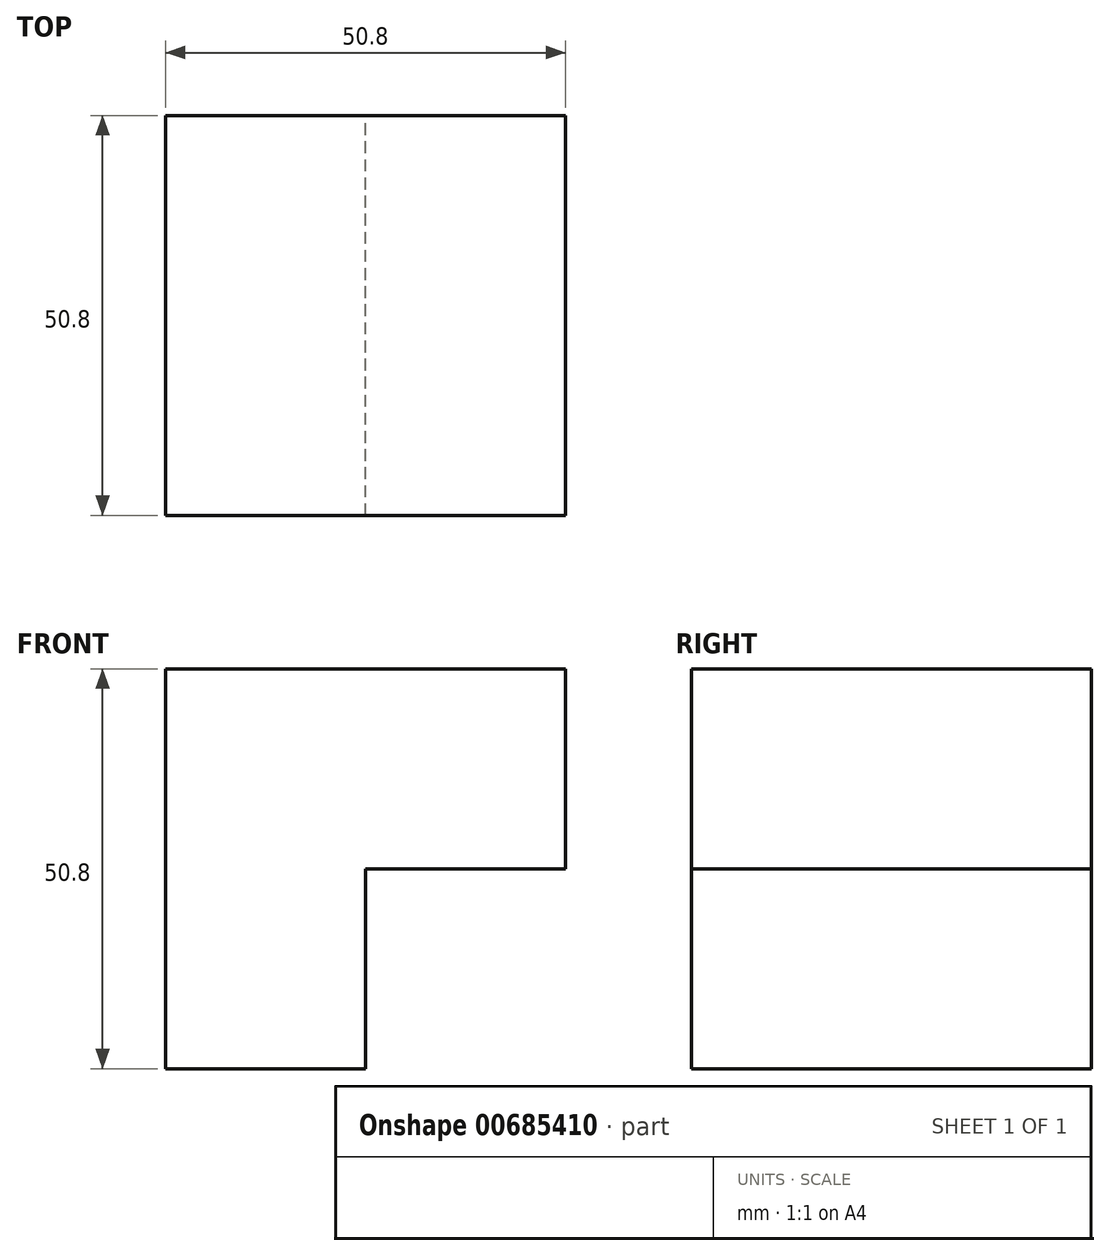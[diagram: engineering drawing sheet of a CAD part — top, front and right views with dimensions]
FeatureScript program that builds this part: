
annotation { "Feature Type Name" : "Feature", "Feature Type Description" : "" }
export const myFeature = defineFeature(function(context is Context, id is Id, definition is map)
    precondition{}
    {
        {
            var Q0;
            Q0=qCreatedBy(makeId("Front.planeOp"),FACE);
            var sketch = newSketch(context, id + "F0", { "sketchPlane" : qUnion([Q0])});
            skLineSegment(sketch, "E0", {"start": v(0, 0) * mm, "end": v(0, 50.8) * mm});
            skLineSegment(sketch, "E1", {"start": v(0, 50.8) * mm, "end": v(50.8, 50.8) * mm});
            skLineSegment(sketch, "E2", {"start": v(50.8, 50.8) * mm, "end": v(50.8, 25.4) * mm});
            skLineSegment(sketch, "E3", {"start": v(50.8, 25.4) * mm, "end": v(25.4, 25.4) * mm});
            skLineSegment(sketch, "E4", {"start": v(25.4, 25.4) * mm, "end": v(25.4, 0) * mm});
            skLineSegment(sketch, "E5", {"start": v(25.4, 0) * mm, "end": v(0, 0) * mm});
            skSolve(sketch);
        }
        {
            var Q0;
            Q0=makeQuery(id+"F0.imprint","IMPRINT",FACE,{"disambiguationData":[TD([[makeQuery(id+"F0.imprint","IMPRINT",EDGE,{"derivedFrom":sQuery(id+"F0.wireOp",EDGE,"E0")}),-1.0]])]});
            extrude(context, id + "F1", {"entities" : qUnion([Q0]), "depth" : 50.8 * mm, "offsetDistance" : 25.4 * mm});
        }
    });
